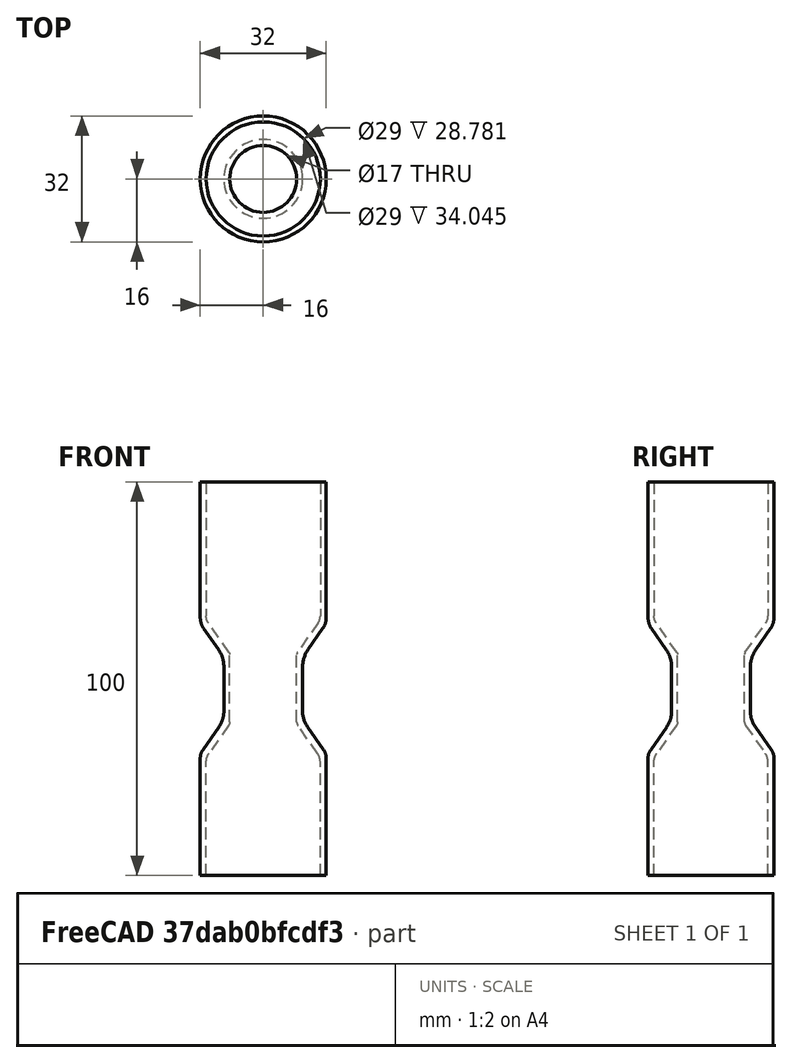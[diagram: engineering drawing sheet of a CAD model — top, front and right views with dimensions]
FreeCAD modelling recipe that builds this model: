
FCSTD DOCUMENT  (FreeCAD 0.20R29177 (Git))
Label: IntestineV2
License: All rights reserved
LicenseURL: http://en.wikipedia.org/wiki/All_rights_reserved
objects: Sketcher::SketchObject×1, Part::Revolution×1, Part::Reverse×1
note: 3 computed .brp shape members not serialized (recipe doc carries the construction recipe); baked Part::Feature solids carry a one-line shape summary decoded from their .brp

FEATURE [Sketcher::SketchObject] Sketch
  FullyConstrained = false
  Placement = pos=(0,0,0) rot=(1,0,0;1.5708rad)
  sketch-geometry (24):
    g0: LineSegment StartX=10 StartY=52.9857 StartZ=0 EndX=10 EndY=41.7483 EndZ=0
    g1: LineSegment StartX=16 StartY=0 StartZ=0 EndX=16 EndY=29.8007 EndZ=0
    g2: LineSegment StartX=16 StartY=0 StartZ=0 EndX=14.5 EndY=0 EndZ=0
    g3: LineSegment StartX=14.5 StartY=0 StartZ=0 EndX=14.5 EndY=28.7815 EndZ=0
    g4: LineSegment StartX=16 StartY=100 StartZ=0 EndX=14.5 EndY=100 EndZ=0
    g5: LineSegment StartX=14.5 StartY=100 StartZ=0 EndX=14.5 EndY=65.9545 EndZ=0
    g6: LineSegment StartX=8.5 StartY=39.0956 StartZ=0 EndX=8.5 EndY=56.1414 EndZ=0
    g7: LineSegment StartX=13.8011 StartY=30.9982 StartZ=0 EndX=8.8021 EndY=38.1374 EndZ=0
    g8: LineSegment StartX=13.9525 StartY=64.2181 StartZ=0 EndX=8.66616 EndY=56.6684 EndZ=0
    g9: LineSegment StartX=11.2501 StartY=37.7836 StartZ=0 EndX=15.3121 EndY=31.9824 EndZ=0
    g10: LineSegment StartX=11.4026 StartY=57.4343 StartZ=0 EndX=15.1218 EndY=62.7458 EndZ=0
    g11: LineSegment StartX=16 StartY=65.5311 StartZ=0 EndX=16 EndY=100 EndZ=0
    g12: ArcOfCircle CenterX=11.144 CenterY=65.5311 CenterZ=0 NormalX=0 NormalY=0 NormalZ=1 AngleXU=0 Radius=4.85596 StartAngle=5.67232 EndAngle=6.28319
    g13: GeomPoint X=16 Y=64 Z=0
    g14: ArcOfCircle CenterX=11.4727 CenterY=65.9545 CenterZ=0 NormalX=0 NormalY=0 NormalZ=1 AngleXU=0 Radius=3.02731 StartAngle=5.67232 EndAngle=6.28319
    g15: GeomPoint X=14.5 Y=65 Z=0
    g16: ArcOfCircle CenterX=12.1963 CenterY=29.8007 CenterZ=0 NormalX=0 NormalY=0 NormalZ=1 AngleXU=0 Radius=3.80374 StartAngle=0 EndAngle=0.610865
    g17: GeomPoint X=16 Y=31 Z=0
    g18: ArcOfCircle CenterX=10.6354 CenterY=28.7815 CenterZ=0 NormalX=0 NormalY=0 NormalZ=1 AngleXU=0 Radius=3.86465 StartAngle=4e-16 EndAngle=0.610865
    g19: GeomPoint X=14.5 Y=30 Z=0
    g20: ArcOfCircle CenterX=17.7558 CenterY=52.9857 CenterZ=0 NormalX=0 NormalY=0 NormalZ=1 AngleXU=0 Radius=7.7558 StartAngle=2.53073 EndAngle=3.14159
    g21: ArcOfCircle CenterX=9.41877 CenterY=56.1414 CenterZ=0 NormalX=0 NormalY=0 NormalZ=1 AngleXU=0 Radius=0.918765 StartAngle=2.53073 EndAngle=3.14159
    g22: ArcOfCircle CenterX=16.9122 CenterY=41.7483 CenterZ=0 NormalX=0 NormalY=0 NormalZ=1 AngleXU=0 Radius=6.91221 StartAngle=3.14159 EndAngle=3.75246
    g23: ArcOfCircle CenterX=10.1705 CenterY=39.0956 CenterZ=0 NormalX=0 NormalY=0 NormalZ=1 AngleXU=0 Radius=1.67045 StartAngle=3.14159 EndAngle=3.75246
  constraints (52):
    c: Vertical(g0)
    c: DistanceX(g-1,g1) = 16
    c: Vertical(g1)
    c: DistanceY(g1,g11) = 100
    c: Perpendicular(g1,g2)
    c: DistanceX(g2,g1) = 1.5
    c: Coincident(g3,g2)
    c: Vertical(g3)
    c: DistanceY(g2,g19) = 30
    c: Coincident(g4,g11)
    c: Horizontal(g4)
    c: DistanceX(g4,g11) = 1.5
    c: Coincident(g5,g4)
    c: Vertical(g5)
    c: DistanceY(g15) = 65
    c: Vertical(g6)
    c: Angle(g7,g6) = 2.53073
    c: Angle(g6,g8) = 2.53073
    c: DistanceY(g2,g-1) = 0
    c: Parallel(g9,g7)
    c: Parallel(g10,g8)
    c: DistanceY(g2,g17) = 31
    c: DistanceY(g2,g13) = 64
    c: DistanceX(g13,g11) = 0
    c: DistanceX(g-1,g4) = 16
    c: PointOnObject(g13,g10)
    c: PointOnObject(g13,g11)
    c: Tangent(g10,g12) = -1.5708
    c: Tangent(g11,g12) = -1.5708
    c: PointOnObject(g15,g5)
    c: PointOnObject(g15,g8)
    c: Tangent(g5,g14) = 1.5708
    c: Tangent(g8,g14) = 1.5708
    c: PointOnObject(g17,g9)
    c: PointOnObject(g17,g1)
    c: Tangent(g9,g16) = 1.5708
    c: Tangent(g1,g16) = -1.5708
    c: PointOnObject(g19,g3)
    c: PointOnObject(g19,g7)
    c: Tangent(g3,g18) = -1.5708
    c: Tangent(g7,g18) = -1.5708
    c: Tangent(g10,g20) = 1.5708
    c: Tangent(g0,g20) = -1.5708
    c: Tangent(g8,g21) = -1.5708
    c: Tangent(g6,g21) = 1.5708
    c: Tangent(g9,g22) = -1.5708
    c: Tangent(g0,g22) = -1.5708
    c: Tangent(g6,g23) = 1.5708
    c: Tangent(g7,g23) = 1.5708
    c: DistanceX(g-1,g0) = 10
    c: DistanceX(g6,g0) = 1.5
    c: DistanceY(g2,g1) = 0
FEATURE [Part::Revolution] Revolve
  Angle = 360
  Axis = (0,0,1)
  Base = (0,0,0)
  FaceMakerClass = Part::FaceMakerBullseye
  Solid = false
  Source = -> Sketch
  Symmetric = false
FEATURE [Part::Reverse] Revolve_rev  label="Revolve (Rev)"
  Source = -> Revolve
